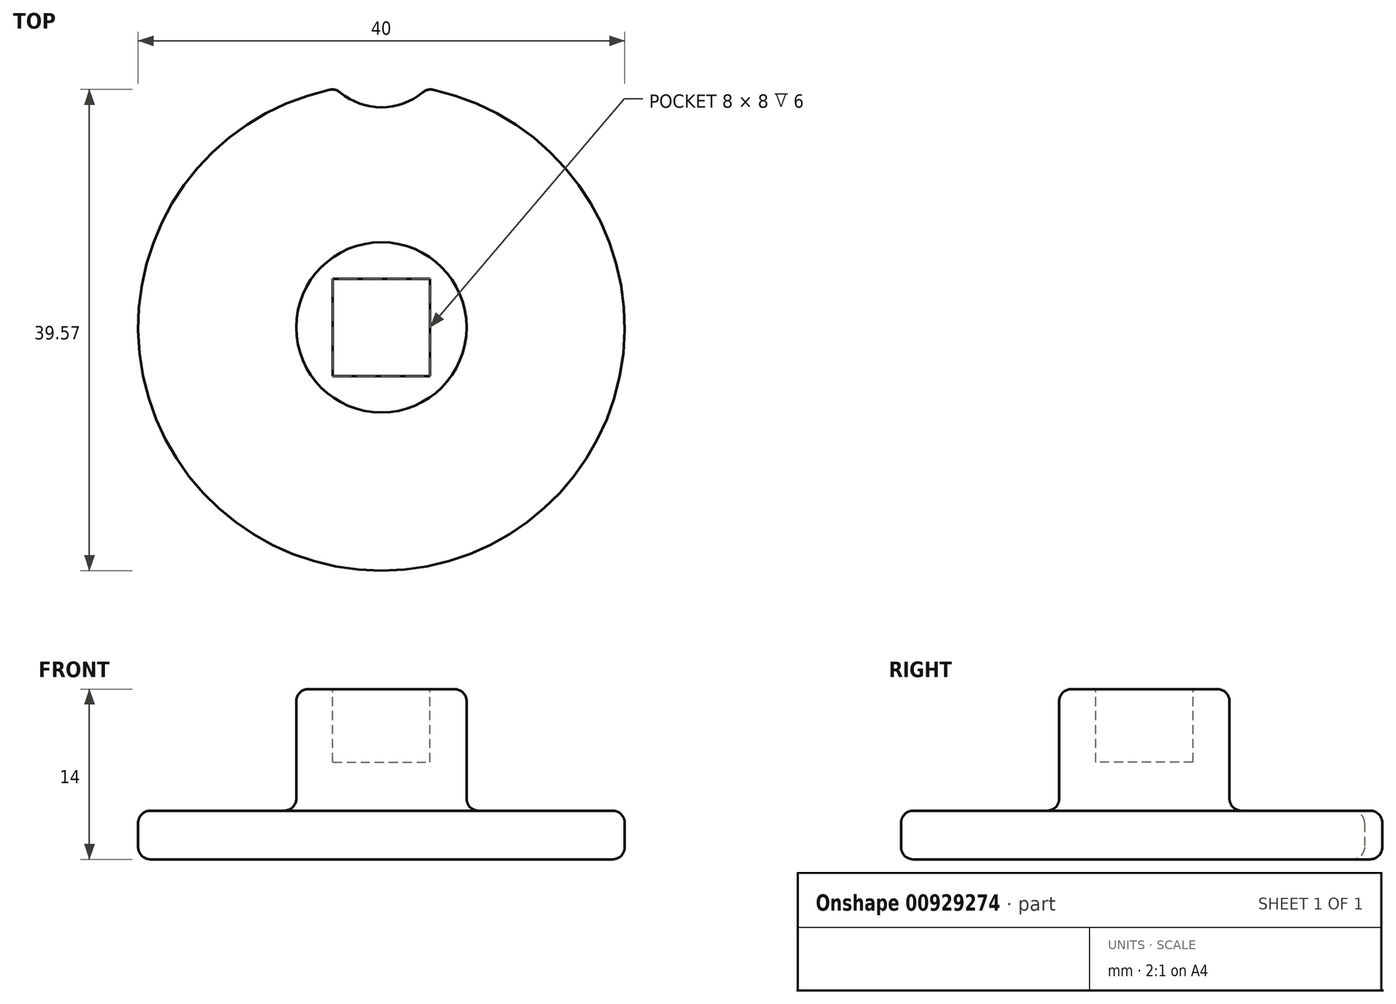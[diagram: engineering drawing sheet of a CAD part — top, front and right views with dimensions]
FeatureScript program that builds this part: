
annotation { "Feature Type Name" : "Feature", "Feature Type Description" : "" }
export const myFeature = defineFeature(function(context is Context, id is Id, definition is map)
    precondition{}
    {
        {
            var Q0;
            Q0=qCreatedBy(makeId("Front.planeOp"),FACE);
            var sketch = newSketch(context, id + "F0", { "sketchPlane" : qUnion([Q0])});
            skLineSegment(sketch, "E0.bottom", {"start": v(0, 0) * mm, "end": v(20, 0) * mm});
            skLineSegment(sketch, "E0.top", {"start": v(0, 4) * mm, "end": v(20, 4) * mm});
            skLineSegment(sketch, "E0.left", {"start": v(0, 0) * mm, "end": v(0, 4) * mm});
            skLineSegment(sketch, "E0.right", {"start": v(20, 0) * mm, "end": v(20, 4) * mm});
            skLineSegment(sketch, "E1.bottom", {"start": v(0, 4) * mm, "end": v(7, 4) * mm});
            skLineSegment(sketch, "E1.top", {"start": v(0, 14) * mm, "end": v(7, 14) * mm});
            skLineSegment(sketch, "E1.left", {"start": v(0, 4) * mm, "end": v(0, 14) * mm});
            skLineSegment(sketch, "E1.right", {"start": v(7, 4) * mm, "end": v(7, 14) * mm});
            skSolve(sketch);
        }
        {
            var Q0;
            Q0=makeQuery(id+"F0.imprint","IMPRINT",FACE,{"disambiguationData":[TD([[makeQuery(id+"F0.imprint","IMPRINT",EDGE,{"derivedFrom":sQuery(id+"F0.wireOp",EDGE,"E1.top")}),-1.0]])]});
            var Q1;
            Q1=makeQuery(id+"F0.imprint","IMPRINT",FACE,{"disambiguationData":[TD([[makeQuery(id+"F0.imprint","IMPRINT",EDGE,{"derivedFrom":sQuery(id+"F0.wireOp",EDGE,"E0.bottom")}),1.0]])]});
            var Q2;
            Q2=sQuery(id+"F0.wireOp",EDGE,"E1.left");
            revolve(context, id + "F1", {"surfaceOperationType" : NewSurfaceOperationType.NEW, "entities" : qUnion([Q0, Q1]), "axis" : qUnion([Q2]), "revolveType" : RevolveType.FULL});
        }
        {
            var Q0;
            Q0=qCreatedBy(makeId("Top.planeOp"),FACE);
            var sketch = newSketch(context, id + "F2", { "sketchPlane" : qUnion([Q0])});
            skCircle(sketch, "E2", {"center": v(0, 23.4) * mm, "radius": 5.3 * mm});
            skSolve(sketch);
        }
        {
            var Q0;
            Q0 = qSketchRegion(id + "F2", true);
            extrude(context, id + "F3", {"entities" : qUnion([Q0]), "operationType" : NewBodyOperationType.REMOVE, "depth" : 25 * mm, "offsetDistance" : 25 * mm});
        }
        {
            var Q0;
            Q0=makeQuery(id+"F3.boolean.opBoolean","COPY",FACE,{"derivedFrom":makeQuery(id+"F3.opExtrude","SWEPT_FACE",FACE,{"disambiguationData":[OSD([sQuery(id+"F2.wireOp",EDGE,"E2")])]})});
            fillet(context, id + "F4", {"entities" : qUnion([Q0]), "radius" : 1 * mm, "tangentPropagation" : true, "allowEdgeOverflow" : false});
        }
        {
            var Q0;
            Q0=makeQuery(id+"F1.opRevolve","SWEPT_EDGE",EDGE,{"disambiguationData":[OSD([sQuery(id+"F0.wireOp",EDGE,"E0.top"),sQuery(id+"F0.wireOp",EDGE,"E0.right")])]});
            var Q1;
            Q1=makeQuery(id+"F1.opRevolve","SWEPT_EDGE",EDGE,{"disambiguationData":[OSD([sQuery(id+"F0.wireOp",EDGE,"E0.bottom"),sQuery(id+"F0.wireOp",EDGE,"E0.right")])]});
            var Q2;
            Q2=makeQuery(id+"F1.opRevolve","SWEPT_EDGE",EDGE,{"disambiguationData":[OSD([sQuery(id+"F0.wireOp",EDGE,"E1.top"),sQuery(id+"F0.wireOp",EDGE,"E1.right")])]});
            var Q3;
            Q3=makeQuery(id+"F1.opRevolve","SWEPT_EDGE",EDGE,{"disambiguationData":[OSD([sQuery(id+"F0.wireOp",EDGE,"E0.top"),sQuery(id+"F0.wireOp",EDGE,"E1.right")])]});
            fillet(context, id + "F5", {"entities" : qUnion([Q0, Q1, Q2, Q3]), "radius" : 1 * mm, "tangentPropagation" : true, "allowEdgeOverflow" : false});
        }
        {
            var Q0;
            Q0=makeQuery(id+"F1.opRevolve","SWEPT_FACE",FACE,{"disambiguationData":[OSD([sQuery(id+"F0.wireOp",EDGE,"E1.top")])]});
            var sketch = newSketch(context, id + "F6", { "sketchPlane" : qUnion([Q0])});
            skLineSegment(sketch, "E3.bottom", {"start": v(-4, 4) * mm, "end": v(4, 4) * mm});
            skLineSegment(sketch, "E3.top", {"start": v(-4, -4) * mm, "end": v(4, -4) * mm});
            skLineSegment(sketch, "E3.left", {"start": v(-4, 4) * mm, "end": v(-4, -4) * mm});
            skLineSegment(sketch, "E3.right", {"start": v(4, 4) * mm, "end": v(4, -4) * mm});
            skSolve(sketch);
        }
        {
            var Q0;
            Q0=makeQuery(id+"F6.imprint","IMPRINT",FACE,{"disambiguationData":[TD([[makeQuery(id+"F6.imprint","IMPRINT",EDGE,{"derivedFrom":sQuery(id+"F6.wireOp",EDGE,"E3.bottom")}),-1.0]])]});
            extrude(context, id + "F7", {"entities" : qUnion([Q0]), "operationType" : NewBodyOperationType.REMOVE, "oppositeDirection" : true, "depth" : 6 * mm, "offsetDistance" : 25 * mm});
        }
    });
